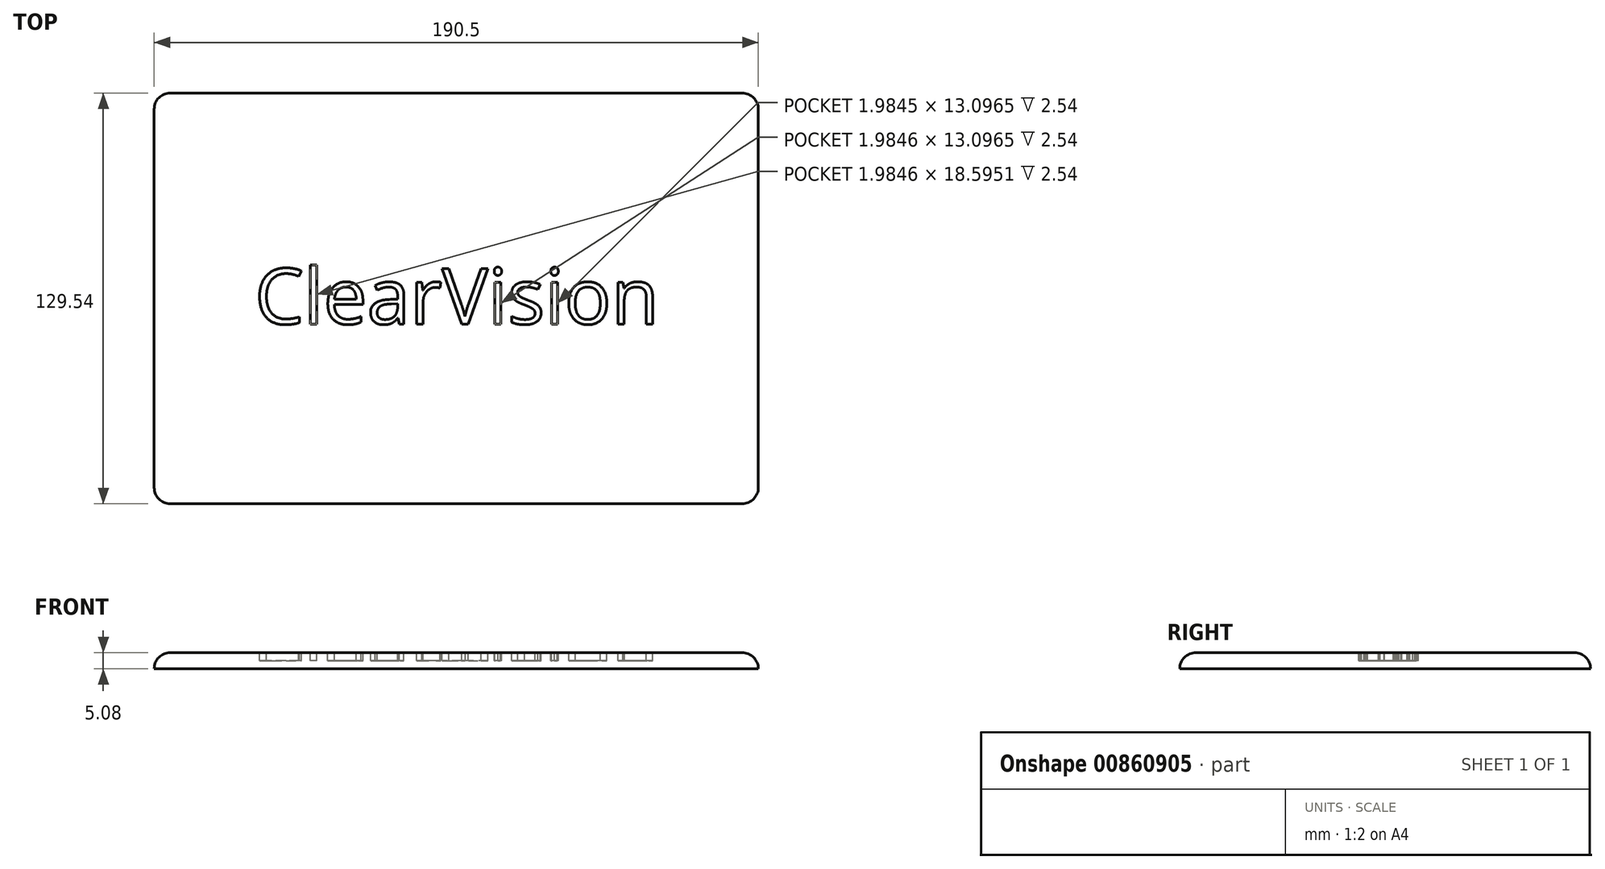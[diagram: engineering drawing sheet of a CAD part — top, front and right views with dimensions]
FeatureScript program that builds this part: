
annotation { "Feature Type Name" : "Feature", "Feature Type Description" : "" }
export const myFeature = defineFeature(function(context is Context, id is Id, definition is map)
    precondition{}
    {
        {
            var Q0;
            Q0=qCreatedBy(makeId("Top.planeOp"),FACE);
            var sketch = newSketch(context, id + "F0", { "sketchPlane" : qUnion([Q0])});
            skLineSegment(sketch, "E0.bottom", {"start": v(-147.94, 64.88) * mm, "end": v(42.56, 64.88) * mm});
            skLineSegment(sketch, "E0.top", {"start": v(-147.94, -64.66) * mm, "end": v(42.56, -64.66) * mm});
            skLineSegment(sketch, "E0.left", {"start": v(-147.94, 64.88) * mm, "end": v(-147.94, -64.66) * mm});
            skLineSegment(sketch, "E0.right", {"start": v(42.56, 64.88) * mm, "end": v(42.56, -64.66) * mm});
            skSolve(sketch);
        }
        {
            var Q0;
            Q0=qSketchRegion(id+"F0",true);
            extrude(context, id + "F1", {"entities" : qUnion([Q0]), "depth" : 5.08 * mm, "offsetDistance" : 25.4 * mm});
        }
        {
            var Q0;
            Q0=makeQuery(id+"F1.opExtrude","CAP_FACE",FACE,{"disambiguationData":[OSD([sQuery(id+"F0.wireOp",EDGE,"E0.bottom"),sQuery(id+"F0.wireOp",EDGE,"E0.top"),sQuery(id+"F0.wireOp",EDGE,"E0.left"),sQuery(id+"F0.wireOp",EDGE,"E0.right")])],"isStart":false});
            var sketch = newSketch(context, id + "F2", { "sketchPlane" : qUnion([Q0])});
            skText(sketch, "E1", { "text": "ClearVision", "fontName": "OpenSans-Regular.ttf"});
            const initialGuessF2  = {"E1": [-0.11619, -0.00798, 1, 0, 0.01762]};
            skSetInitialGuess(sketch, initialGuessF2);
            skSolve(sketch);
        }
        {
            var Q0;
            Q0=qSketchRegion(id+"F2",true);
            extrude(context, id + "F3", {"entities" : qUnion([Q0]), "operationType" : NewBodyOperationType.REMOVE, "oppositeDirection" : true, "depth" : 2.54 * mm, "offsetDistance" : 25.4 * mm});
        }
        {
            var Q0;
            Q0=makeQuery(id+"F1.opExtrude","CAP_EDGE",EDGE,{"disambiguationData":[OSD([sQuery(id+"F0.wireOp",EDGE,"E0.left")])],"isStart":false});
            var Q1;
            Q1=makeQuery(id+"F1.opExtrude","CAP_EDGE",EDGE,{"disambiguationData":[OSD([sQuery(id+"F0.wireOp",EDGE,"E0.top")])],"isStart":false});
            var Q2;
            Q2=makeQuery(id+"F1.opExtrude","CAP_EDGE",EDGE,{"disambiguationData":[OSD([sQuery(id+"F0.wireOp",EDGE,"E0.right")])],"isStart":false});
            var Q3;
            Q3=makeQuery(id+"F1.opExtrude","CAP_EDGE",EDGE,{"disambiguationData":[OSD([sQuery(id+"F0.wireOp",EDGE,"E0.bottom")])],"isStart":false});
            fillet(context, id + "F4", {"entities" : qUnion([Q0, Q1, Q2, Q3]), "radius" : 5.08 * mm, "tangentPropagation" : true, "allowEdgeOverflow" : false});
        }
        {
            var Q0;
            Q0=makeQuery(id+"F4.opFillet","BLEND_EDGE",EDGE,{"blendedFrom":[makeQuery(id+"F1.opExtrude","CAP_EDGE",EDGE,{"disambiguationData":[OSD([sQuery(id+"F0.wireOp",EDGE,"E0.top")])],"isStart":false}),makeQuery(id+"F1.opExtrude","CAP_EDGE",EDGE,{"disambiguationData":[OSD([sQuery(id+"F0.wireOp",EDGE,"E0.left")])],"isStart":false})],"blendedInto":[]});
            var Q1;
            Q1=makeQuery(id+"F4.opFillet","BLEND_EDGE",EDGE,{"blendedFrom":[makeQuery(id+"F1.opExtrude","CAP_EDGE",EDGE,{"disambiguationData":[OSD([sQuery(id+"F0.wireOp",EDGE,"E0.top")])],"isStart":false}),makeQuery(id+"F1.opExtrude","CAP_EDGE",EDGE,{"disambiguationData":[OSD([sQuery(id+"F0.wireOp",EDGE,"E0.right")])],"isStart":false})],"blendedInto":[]});
            var Q2;
            Q2=makeQuery(id+"F4.opFillet","BLEND_EDGE",EDGE,{"blendedFrom":[makeQuery(id+"F1.opExtrude","CAP_EDGE",EDGE,{"disambiguationData":[OSD([sQuery(id+"F0.wireOp",EDGE,"E0.bottom")])],"isStart":false}),makeQuery(id+"F1.opExtrude","CAP_EDGE",EDGE,{"disambiguationData":[OSD([sQuery(id+"F0.wireOp",EDGE,"E0.right")])],"isStart":false})],"blendedInto":[]});
            var Q3;
            Q3=makeQuery(id+"F4.opFillet","BLEND_EDGE",EDGE,{"blendedFrom":[makeQuery(id+"F1.opExtrude","CAP_EDGE",EDGE,{"disambiguationData":[OSD([sQuery(id+"F0.wireOp",EDGE,"E0.bottom")])],"isStart":false}),makeQuery(id+"F1.opExtrude","CAP_EDGE",EDGE,{"disambiguationData":[OSD([sQuery(id+"F0.wireOp",EDGE,"E0.left")])],"isStart":false})],"blendedInto":[]});
            fillet(context, id + "F5", {"entities" : qUnion([Q0, Q1, Q2, Q3]), "radius" : 5.08 * mm, "tangentPropagation" : true, "allowEdgeOverflow" : false});
        }
    });
